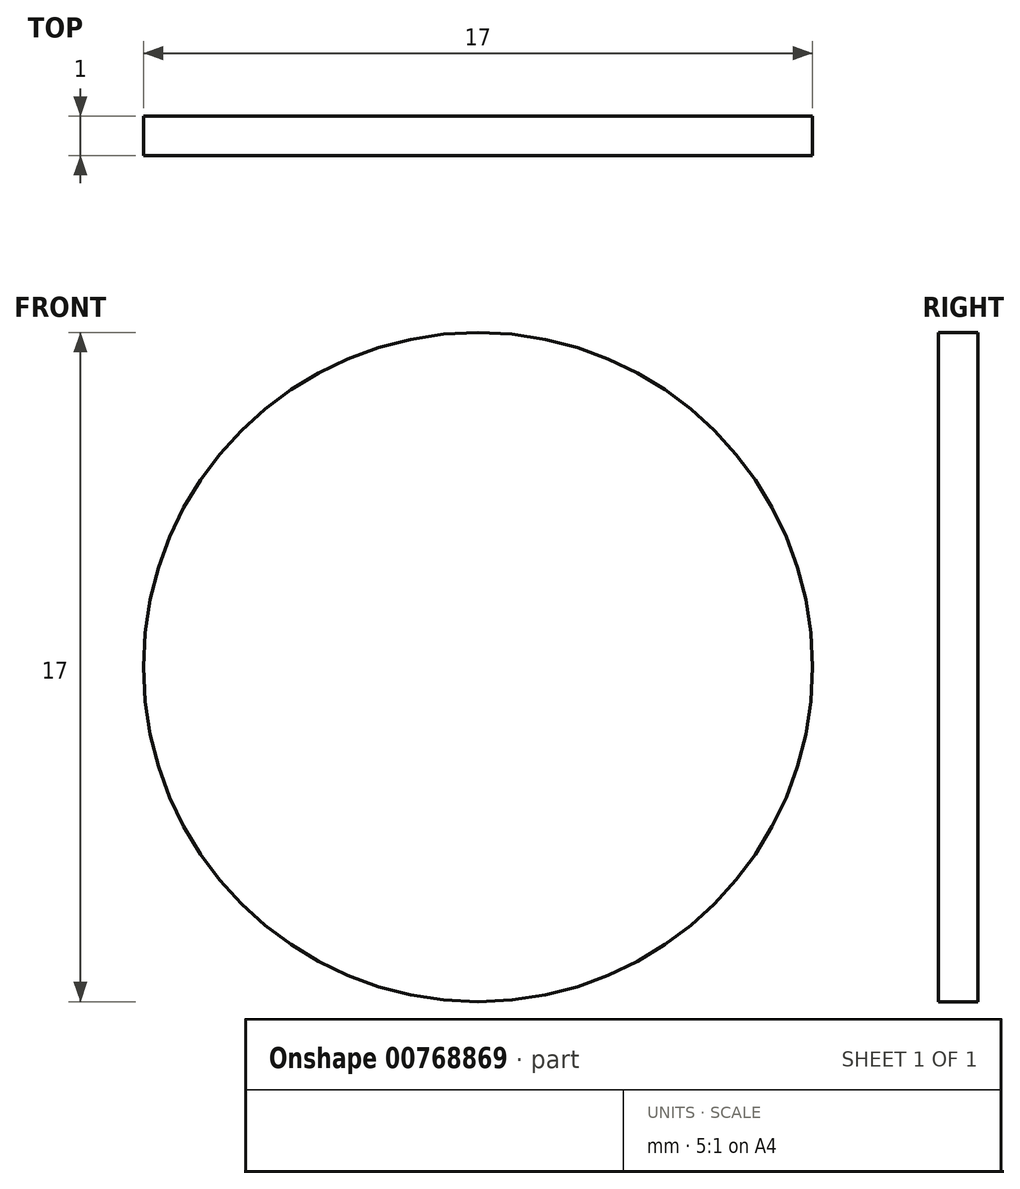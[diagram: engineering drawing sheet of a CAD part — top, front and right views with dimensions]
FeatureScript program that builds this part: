
annotation { "Feature Type Name" : "Feature", "Feature Type Description" : "" }
export const myFeature = defineFeature(function(context is Context, id is Id, definition is map)
    precondition{}
    {
        {
            var Q0;
            Q0=qCreatedBy(makeId("Front.planeOp"),FACE);
            var sketch = newSketch(context, id + "F0", { "sketchPlane" : qUnion([Q0])});
            skCircle(sketch, "E0", {"center": v(0, 0) * mm, "radius": 8.5 * mm});
            skSolve(sketch);
        }
        {
            var Q0;
            Q0 = qSketchRegion(id + "F0", true);
            extrude(context, id + "F1", {"entities" : qUnion([Q0]), "depth" : 1 * mm, "offsetDistance" : 25 * mm});
        }
    });
